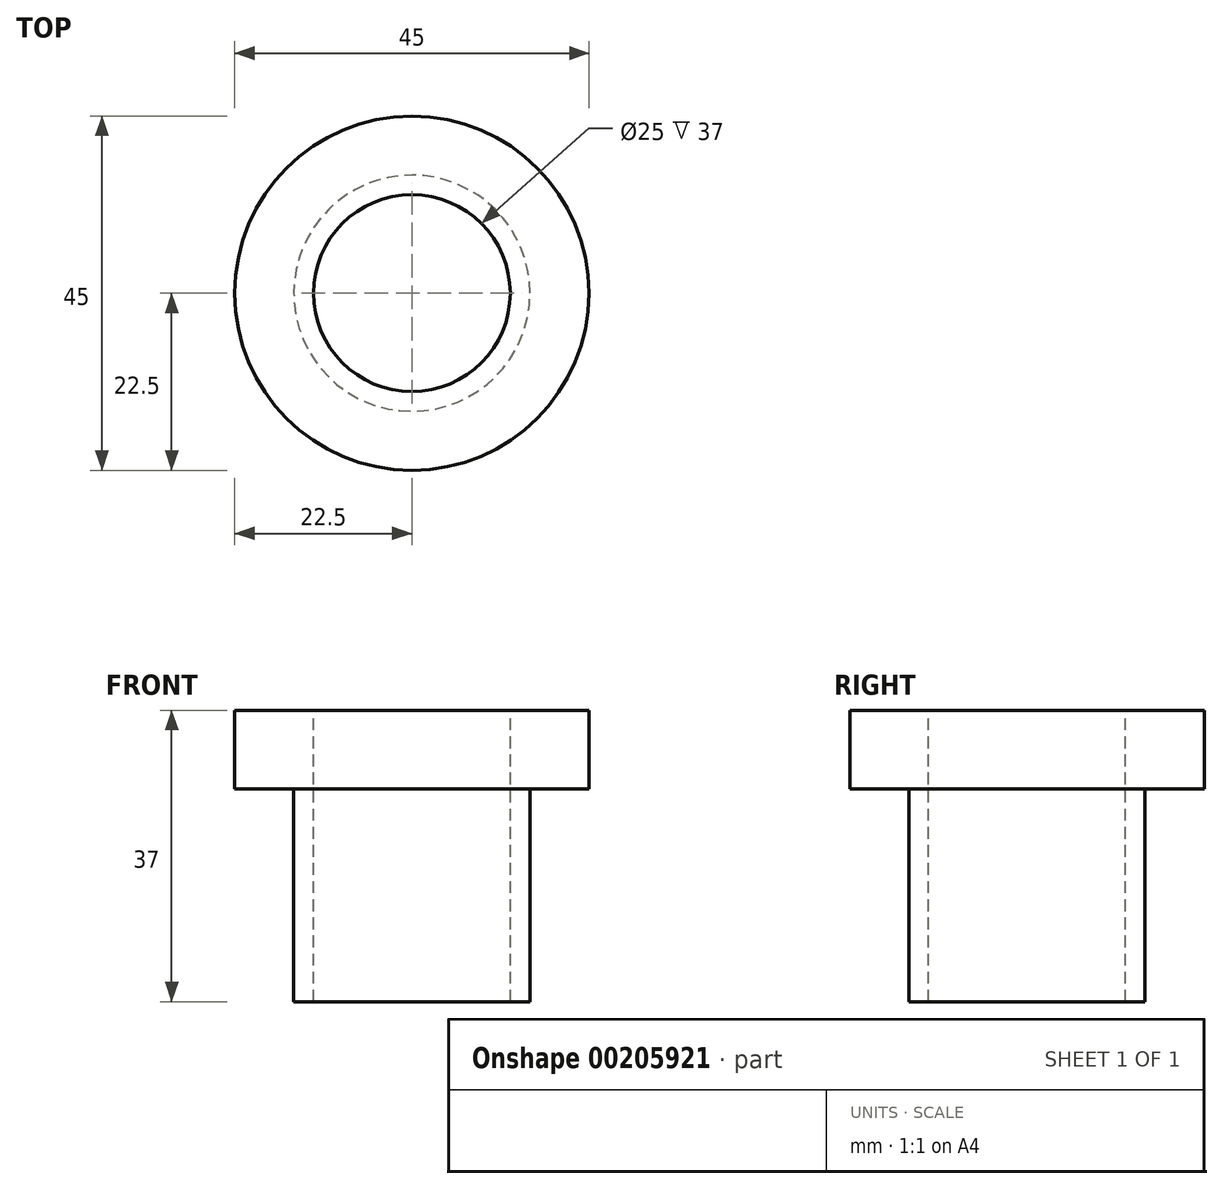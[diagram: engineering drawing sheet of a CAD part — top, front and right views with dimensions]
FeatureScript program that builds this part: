
annotation { "Feature Type Name" : "Feature", "Feature Type Description" : "" }
export const myFeature = defineFeature(function(context is Context, id is Id, definition is map)
    precondition{}
    {
        {
            var Q0;
            Q0=qCreatedBy(makeId("Top.planeOp"),FACE);
            var sketch = newSketch(context, id + "F0", { "sketchPlane" : qUnion([Q0])});
            skCircle(sketch, "E0", {"center": v(0, 0) * mm, "radius": 22.5 * mm});
            skSolve(sketch);
        }
        {
            var Q0;
            Q0 = qSketchRegion(id + "F0", true);
            extrude(context, id + "F1", {"entities" : qUnion([Q0]), "oppositeDirection" : true, "depth" : 10 * mm});
        }
        {
            var Q0;
            Q0=makeQuery(id+"F1.opExtrude","CAP_FACE",FACE,{"disambiguationData":[OSD([sQuery(id+"F0.wireOp",EDGE,"E0")])],"isStart":true});
            var sketch = newSketch(context, id + "F2", { "sketchPlane" : qUnion([Q0])});
            skCircle(sketch, "E1", {"center": v(0, 0) * mm, "radius": 15 * mm});
            skSolve(sketch);
        }
        {
            var Q0;
            Q0=makeQuery(id+"F2.imprint","IMPRINT",FACE,{"disambiguationData":[TD([[makeQuery(id+"F2.imprint","IMPRINT",EDGE,{"derivedFrom":sQuery(id+"F2.wireOp",EDGE,"E1")}),1.0]])]});
            extrude(context, id + "F3", {"entities" : qUnion([Q0]), "operationType" : NewBodyOperationType.ADD, "oppositeDirection" : true, "depth" : 37 * mm});
        }
        {
            var Q0;
            Q0=qCreatedBy(makeId("Top.planeOp"),FACE);
            var sketch = newSketch(context, id + "F4", { "sketchPlane" : qUnion([Q0])});
            skCircle(sketch, "E2", {"center": v(0, 0) * mm, "radius": 12.5 * mm});
            skSolve(sketch);
        }
        {
            var Q0;
            Q0=makeQuery(id+"F4.imprint","IMPRINT",FACE,{"disambiguationData":[TD([[makeQuery(id+"F4.imprint","IMPRINT",EDGE,{"derivedFrom":sQuery(id+"F4.wireOp",EDGE,"E2")}),1.0]])]});
            var Q1;
            Q1=sQuery(id+"F4.wireOp",EDGE,"E2");
            extrude(context, id + "F5", {"entities" : qUnion([Q0]), "operationType" : NewBodyOperationType.REMOVE, "surfaceEntities" : qUnion([Q1]), "oppositeDirection" : true, "depth" : 37 * mm});
        }
    });
